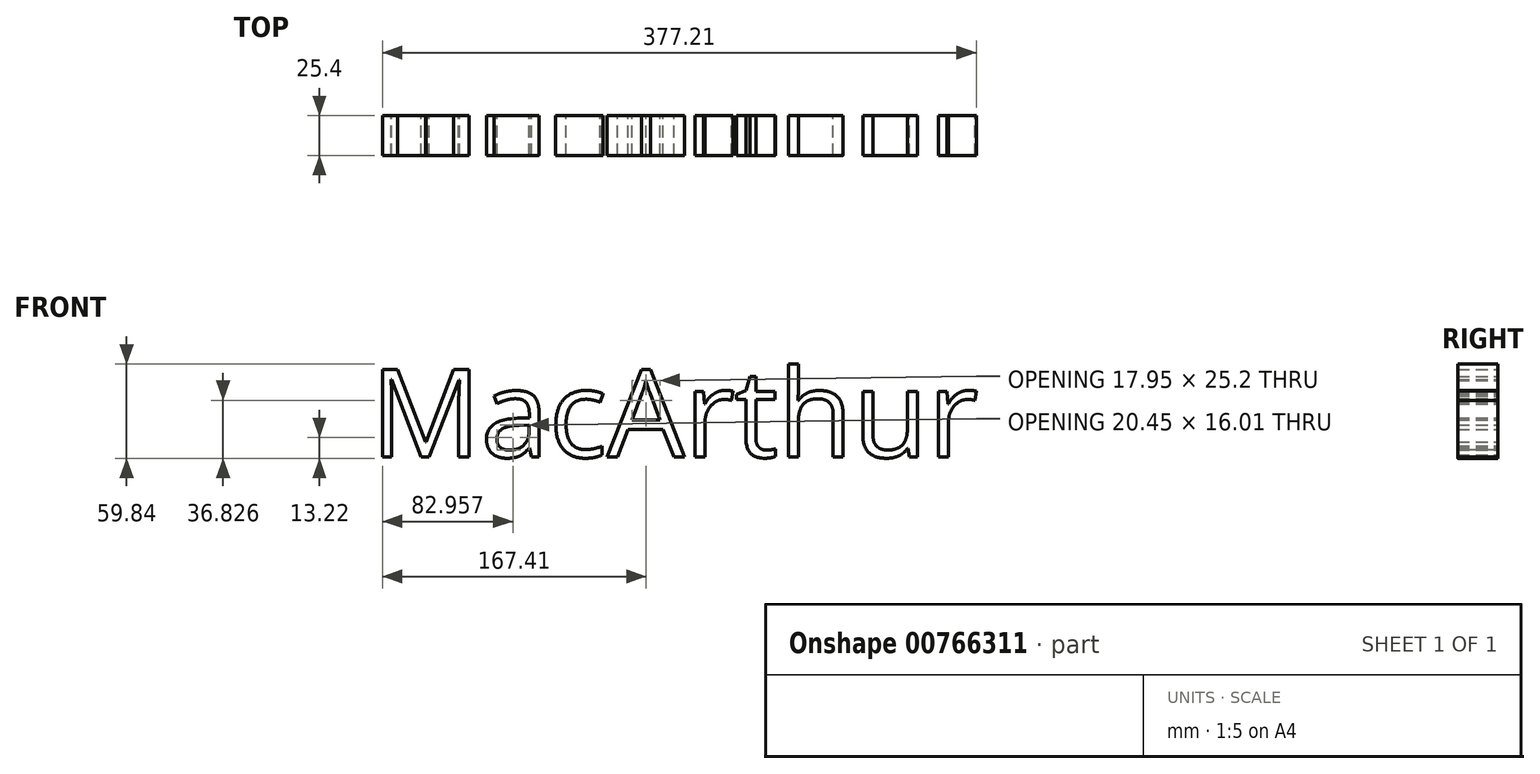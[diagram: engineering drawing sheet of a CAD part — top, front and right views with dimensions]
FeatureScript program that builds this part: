
annotation { "Feature Type Name" : "Feature", "Feature Type Description" : "" }
export const myFeature = defineFeature(function(context is Context, id is Id, definition is map)
    precondition{}
    {
        {
            var Q0;
            Q0=qCreatedBy(makeId("Front.planeOp"),FACE);
            var sketch = newSketch(context, id + "F0", { "sketchPlane" : qUnion([Q0])});
            skText(sketch, "E0", { "text": "MacArthur", "fontName": "OpenSans-Regular.ttf"});
            const initialGuessF0  = {"E0": [-0.2057, -0.0066, 1, 0, 0.05597]};
            skSetInitialGuess(sketch, initialGuessF0);
            skSolve(sketch);
        }
        {
            var Q0;
            Q0 = qSketchRegion(id + "F0", true);
            extrude(context, id + "F1", {"entities" : qUnion([Q0]), "depth" : 25.4 * mm, "offsetDistance" : 25.4 * mm});
        }
    });
